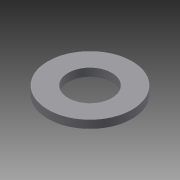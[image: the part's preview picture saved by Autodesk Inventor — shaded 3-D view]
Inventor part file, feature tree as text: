
AUTODESK INVENTOR PART (.ipt)
format: ipt  version: 2013 (Build 170138000, 138)  size: 73,216 bytes
history: native  units: mm
features: extrude x1, sketch x1
ambient origin geometry x8: Origin, YZ Plane, XZ Plane, XY Plane, X Axis, Y Axis, Z Axis, Center Point
bodies: Solid1 (feature_tree)
feature tree (2):
  extrude  "Extrusion1"  Depth=16.0mm
  sketch  "Sketch1"  dims[d0=8.3mm d2=16.0mm d3=1.5mm d4=0.0mm]
